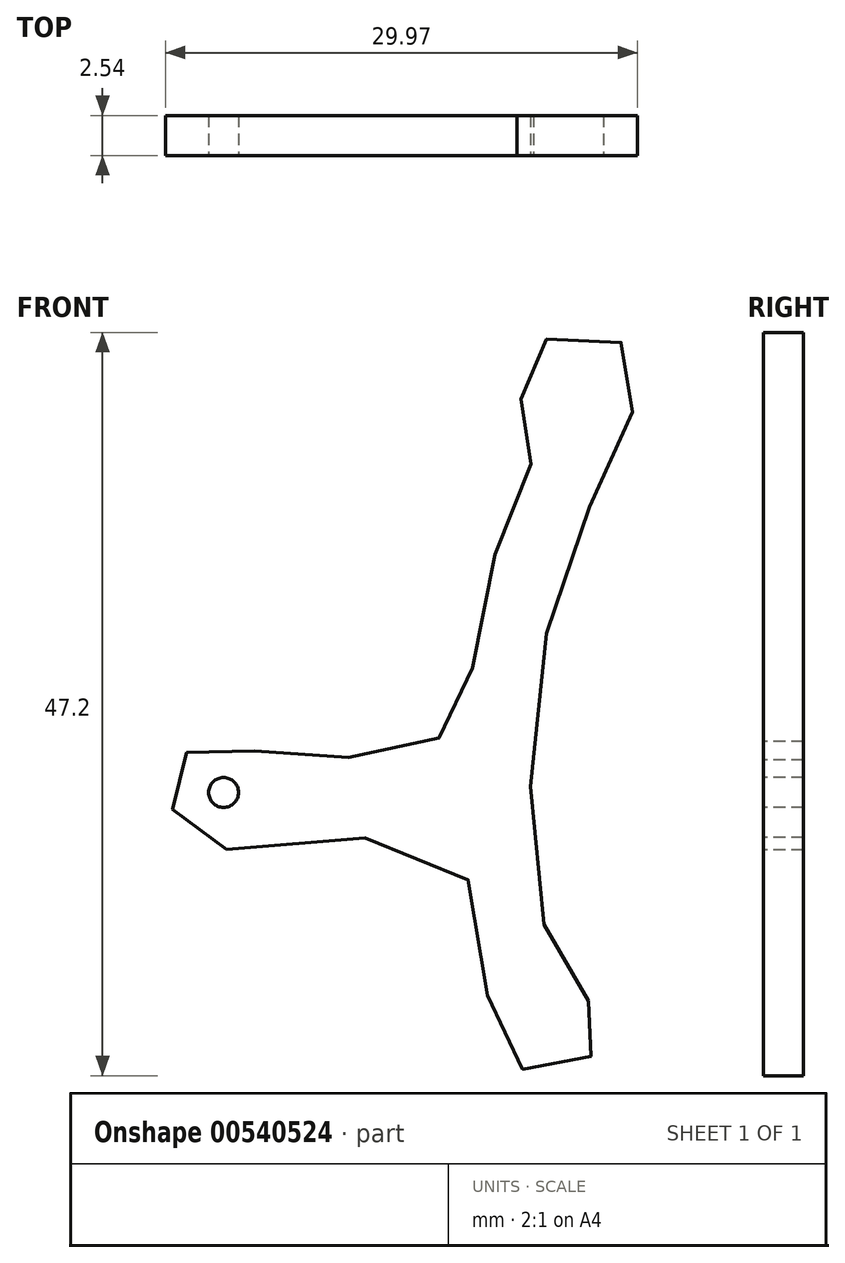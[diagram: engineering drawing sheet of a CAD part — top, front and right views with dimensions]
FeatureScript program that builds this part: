
annotation { "Feature Type Name" : "Feature", "Feature Type Description" : "" }
export const myFeature = defineFeature(function(context is Context, id is Id, definition is map)
    precondition{}
    {
        {
            var Q0;
            Q0=qCreatedBy(makeId("Front.planeOp"),FACE);
            var sketch = newSketch(context, id + "F0", { "sketchPlane" : qUnion([Q0])});
            skFitSpline(sketch, "E0", {"points": [v(-25.6, -21.61) * mm, v(-11.94, -21.61) * mm, v(-9.1, -30.34) * mm, v(-7.02, -35.45) * mm, v(-3.22, -35.45) * mm, v(-1.7, -32.42) * mm, v(-3.8, -30.15) * mm, v(-6.26, -19.9) * mm, v(-3.98, -3.22) * mm, v(0, 5.5) * mm, v(0, 10.05) * mm, v(-3.41, 11.19) * mm, v(-7.02, 9.3) * mm, v(-6.26, 4.93) * mm, v(-6.45, 2.28) * mm, v(-9.48, -6.07) * mm, v(-10.8, -13.46) * mm, v(-14.98, -15.36) * mm, v(-22.56, -15.74) * mm, v(-26.54, -14.79) * mm, v(-29.39, -17.06) * mm, v(-28.63, -19.72) * mm, v(-25.6, -21.61) * mm]});
            skCircle(sketch, "E1", {"center": v(-25.79, -18.01) * mm, "radius": 0.95 * mm});
            skSolve(sketch);
        }
        {
            var Q0;
            Q0=sQuery(id+"F0.wireOp",EDGE,"E0");
            var Q1;
            Q1=sQuery(id+"F0.wireOp",EDGE,"E1");
            extrude(context, id + "F1", {"bodyType" : ToolBodyType.SURFACE, "surfaceEntities" : qUnion([Q0, Q1]), "depth" : 2.54 * mm, "offsetDistance" : 25.4 * mm});
        }
    });
